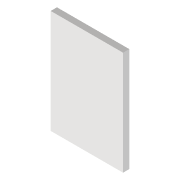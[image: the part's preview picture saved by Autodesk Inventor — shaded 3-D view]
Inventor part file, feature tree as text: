
AUTODESK INVENTOR PART (.ipt)
format: ipt  version: 2022 (Build 260153000, 153)  size: 102,400 bytes
history: native  units: mm
features: extrude x3, sketch x3, reference x3, other x3, projected_geometry x2
ambient origin geometry x8: Origin, YZ Plane, XZ Plane, XY Plane, X Axis, Y Axis, Z Axis, Center Point
bodies: Volumenkörper1 (feature_tree)
feature tree (14):
  extrude  "Extrusion1"  Depth=25.0mm
  extrude  "Extrusion2"  Depth=1.5mm TaperAngle=0.0deg
  extrude  "Extrusion3"  Depth=10.0mm TaperAngle=0.0deg
  sketch  "Skizze1"  dims[d0=21.0mm d1=25.0mm]
  reference  "Referenz1"
  sketch  "Skizze2"  dims[d2=3.6mm d4=1.5mm d5=0.0mm]
  reference  "Referenz2"
  projected_geometry  "Projizierte Kontur1"
  reference  "Referenz3"
  sketch  "Skizze3"  dims[d6=1.75mm d7=10.0mm d8=0.0mm d9=10.0mm d10=0.0mm]
  projected_geometry  "Projizierte Kontur2"
  other  "<userpath>\Documents\GitHub\Guinardia\INVENTOR\Assembly_Huawei_P30_Scanninglens.iam"
  other  "Assembly_Huawei_P30_Scanninglens.iam"
  other  "00_huawei_p30_Objectivelensassembly:1"
